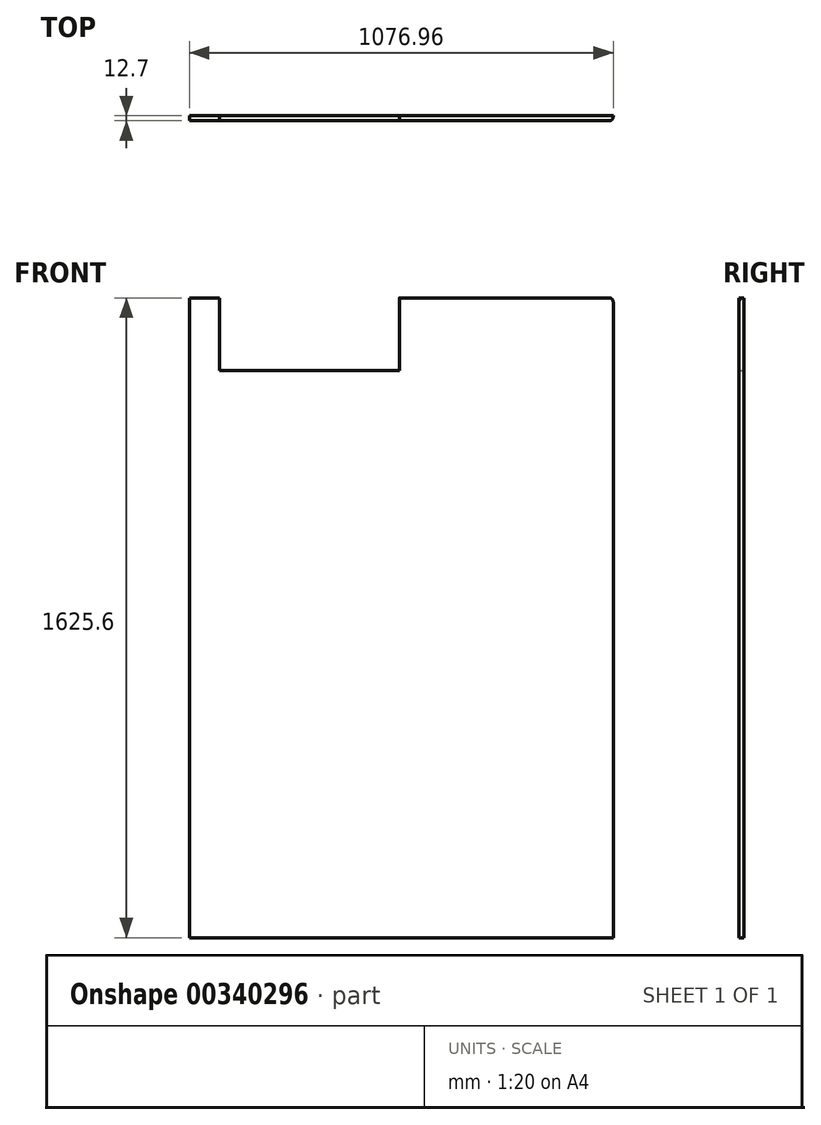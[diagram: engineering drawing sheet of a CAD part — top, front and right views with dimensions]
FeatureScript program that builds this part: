
annotation { "Feature Type Name" : "Feature", "Feature Type Description" : "" }
export const myFeature = defineFeature(function(context is Context, id is Id, definition is map)
    precondition{}
    {
        {
            var Q0;
            Q0=qCreatedBy(makeId("Front.planeOp"),FACE);
            var sketch = newSketch(context, id + "F0", { "sketchPlane" : qUnion([Q0])});
            skLineSegment(sketch, "E0.bottom", {"start": v(538.48, -812.8) * mm, "end": v(-538.48, -812.8) * mm});
            skLineSegment(sketch, "E0.top", {"start": v(538.48, 812.8) * mm, "end": v(-5.08, 812.8) * mm});
            skLineSegment(sketch, "E0.left", {"start": v(538.48, -812.8) * mm, "end": v(538.48, 812.8) * mm});
            skLineSegment(sketch, "E0.right", {"start": v(-538.48, -812.8) * mm, "end": v(-538.48, 812.8) * mm});
            skPoint(sketch, "E0.middle", {"position": v(0, 0) * mm});
            skLineSegment(sketch, "E1", {"start": v(-538.48, 812.8) * mm, "end": v(-462.28, 812.8) * mm, "construction": true});
            skLineSegment(sketch, "E2.top", {"start": v(-462.28, 628.65) * mm, "end": v(-5.08, 628.65) * mm});
            skLineSegment(sketch, "E2.left", {"start": v(-462.28, 812.8) * mm, "end": v(-462.28, 628.65) * mm});
            skLineSegment(sketch, "E2.right", {"start": v(-5.08, 812.8) * mm, "end": v(-5.08, 628.65) * mm});
            skLineSegment(sketch, "E3.trimOffspring", {"start": v(-462.28, 812.8) * mm, "end": v(-538.48, 812.8) * mm});
            skSolve(sketch);
        }
        {
            var Q0;
            Q0=qSketchRegion(id+"F0",true);
            extrude(context, id + "F1", {"entities" : qUnion([Q0]), "depth" : 12.7 * mm});
        }
        {
            var Q0;
            Q0=makeQuery(id+"F1.opExtrude","CAP_EDGE",EDGE,{"disambiguationData":[OSD([sQuery(id+"F0.wireOp",EDGE,"E0.top")])],"isStart":false});
            fillet(context, id + "F2", {"entities" : qUnion([Q0]), "radius" : 10.16 * mm, "tangentPropagation" : true, "allowEdgeOverflow" : false});
        }
        {
            var Q0;
            Q0=makeQuery(id+"F1.opExtrude","CAP_EDGE",EDGE,{"disambiguationData":[OSD([sQuery(id+"F0.wireOp",EDGE,"E0.left")])],"isStart":false});
            fillet(context, id + "F3", {"entities" : qUnion([Q0]), "radius" : 10.16 * mm, "tangentPropagation" : true, "allowEdgeOverflow" : false});
        }
    });
